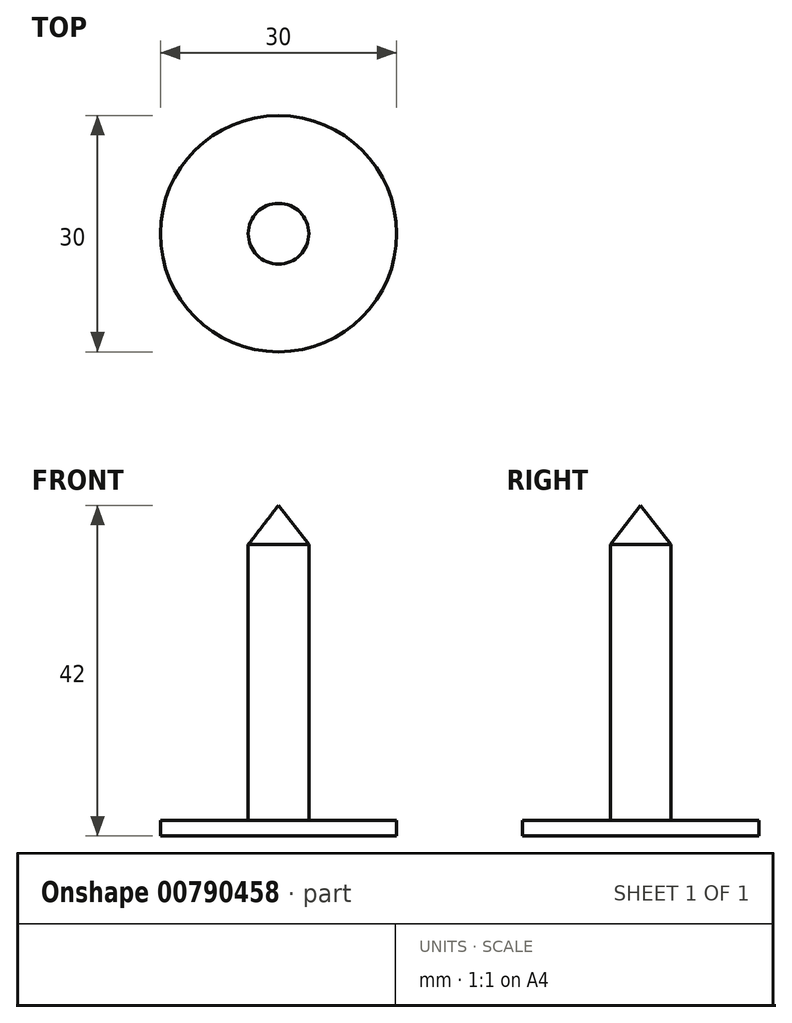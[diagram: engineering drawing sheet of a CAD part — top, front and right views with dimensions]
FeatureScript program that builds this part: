
annotation { "Feature Type Name" : "Feature", "Feature Type Description" : "" }
export const myFeature = defineFeature(function(context is Context, id is Id, definition is map)
    precondition{}
    {
        {
            var Q0;
            Q0=qCreatedBy(makeId("Front.planeOp"),FACE);
            var sketch = newSketch(context, id + "F0", { "sketchPlane" : qUnion([Q0])});
            skLineSegment(sketch, "E0", {"start": v(0, 0) * mm, "end": v(0, 101.2) * mm, "construction": true});
            skLineSegment(sketch, "E1", {"start": v(-3.85, 48.45) * mm, "end": v(-3.85, 43.45) * mm});
            skLineSegment(sketch, "E2.trimOffspring", {"start": v(-3.85, 33.45) * mm, "end": v(-3.85, 13.45) * mm});
            skLineSegment(sketch, "E3", {"start": v(-3.85, 13.45) * mm, "end": v(0, 13.45) * mm});
            skLineSegment(sketch, "E4.bottom", {"start": v(0, 13.45) * mm, "end": v(-15, 13.45) * mm});
            skLineSegment(sketch, "E4.top", {"start": v(0, 13.45) * mm, "end": v(-15, 13.45) * mm});
            skLineSegment(sketch, "E4.left", {"start": v(0, 13.45) * mm, "end": v(0, 13.45) * mm});
            skLineSegment(sketch, "E4.right", {"start": v(-15, 13.45) * mm, "end": v(-15, 13.45) * mm});
            skLineSegment(sketch, "E5", {"start": v(0, 53.45) * mm, "end": v(0, 13.45) * mm});
            skLineSegment(sketch, "E6", {"start": v(-15, 13.45) * mm, "end": v(-15, 11.45) * mm});
            skLineSegment(sketch, "E7", {"start": v(-15, 11.45) * mm, "end": v(0, 11.45) * mm});
            skLineSegment(sketch, "E8.bottom", {"start": v(-15, 13.45) * mm, "end": v(0, 13.45) * mm});
            skLineSegment(sketch, "E8.right", {"start": v(0, 13.45) * mm, "end": v(0, 11.45) * mm});
            skLineSegment(sketch, "E9", {"start": v(-3.85, 43.45) * mm, "end": v(-3.85, 33.45) * mm});
            skLineSegment(sketch, "E10", {"start": v(0, 53.45) * mm, "end": v(-3.85, 48.45) * mm});
            skSolve(sketch);
        }
        {
            var Q0;
            {var subQ5=sQuery(id+"F0.wireOp",EDGE,"E4.right");Q0=makeQuery(id+"F0.imprint","IMPRINT",FACE,{"disambiguationData":[TD([[makeQuery(id+"F0.imprint","IMPRINT",EDGE,{"derivedFrom":subQ5}),-1.0]])]});}
            var Q1;
            {var subQ5=sQuery(id+"F0.wireOp",EDGE,"E4.left");Q1=makeQuery(id+"F0.imprint","IMPRINT",FACE,{"disambiguationData":[TD([[makeQuery(id+"F0.imprint","IMPRINT",EDGE,{"derivedFrom":subQ5}),1.0]])]});}
            var Q2;
            Q2=makeQuery(id+"F0.imprint","IMPRINT",FACE,{"disambiguationData":[TD([[makeQuery(id+"F0.imprint","IMPRINT",EDGE,{"derivedFrom":sQuery(id+"F0.wireOp",EDGE,"E1")}),1.0]])]});
            var Q3;
            Q3=makeQuery(id+"F0.imprint","IMPRINT",FACE,{"disambiguationData":[TD([[makeQuery(id+"F0.imprint","IMPRINT",EDGE,{"derivedFrom":sQuery(id+"F0.wireOp",EDGE,"E7")}),1.0]])]});
            var Q4;
            {var subQ0=sQuery(id+"F0.wireOp",EDGE,"z0dVPFTq-MBpH-tm1F-sQ5P-HKkLjGr0qIY8");Q4=makeQuery(id+"F0.imprint","IMPRINT",FACE,{"disambiguationData":[TD([[makeQuery(id+"F0.imprint","IMPRINT",EDGE,{"derivedFrom":subQ0}),-1.0]])]});}
            var Q5;
            {var subQ3=sQuery(id+"F0.wireOp",EDGE,"mHctbxaU-HMjW-Bu9p-vV60-hWhE2YjFO5Uf");Q5=makeQuery(id+"F0.imprint","IMPRINT",FACE,{"disambiguationData":[TD([[makeQuery(id+"F0.imprint","IMPRINT",EDGE,{"derivedFrom":subQ3}),-1.0]])]});}
            var Q6;
            Q6=sQuery(id+"F0.wireOp",EDGE,"E0");
            revolve(context, id + "F1", {"surfaceOperationType" : NewSurfaceOperationType.NEW, "entities" : qUnion([Q0, Q1, Q2, Q3, Q4, Q5]), "axis" : qUnion([Q6]), "revolveType" : RevolveType.FULL});
        }
    });
